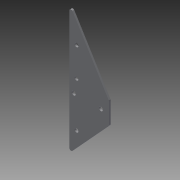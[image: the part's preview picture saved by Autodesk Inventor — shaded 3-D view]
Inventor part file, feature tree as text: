
AUTODESK INVENTOR PART (.ipt)
format: ipt  version: 2013 (Build 170138000, 138)  size: 130,560 bytes
history: native  units: in
note: dims shown in document units (in); Inventor stores cm internally (conversion verified against a paired STEP export)
features: extrude x5, sketch x5, fillet x3
ambient origin geometry x8: Origin, YZ Plane, XZ Plane, XY Plane, X Axis, Y Axis, Z Axis, Center Point
bodies: Solid1 (feature_tree)
feature tree (13):
  extrude  "Extrusion1"  Depth=6.0in
  extrude  "Extrusion2"  Depth=0.28in
  fillet  "Fillet1"  Radius=0.28in
  extrude  "Extrusion3"  Depth=0.75in
  fillet  "Fillet2"  Radius=0.56in
  fillet  "Fillet3"  Radius=0.31in
  extrude  "Extrusion4"  Depth=0.125in
  extrude  "Extrusion5"  Depth=0.266in
  sketch  "Sketch1"  dims[d1=1.5in d2=6.0in]
  sketch  "Sketch2"  dims[d3=0.125in d4=0.0in d5=0.28in d6=0.28in]
  sketch  "Sketch3"  dims[d7=0.75in d8=0.75in d9=0.56in d11=0.31in]
  sketch  "Sketch4"  dims[d12=1.0in d13=0.0in d14=0.125in]
  sketch  "Sketch5"  dims[d15=0.266in d16=0.266in d17=0.5in d18=0.5in d19=1.737in d20=2.0in d21=1.0in d22=0.0in d23=0.125in d24=3.0in d25=2.75in d26=2.75in d27=0.125in d28=0.266in d29=3.125in d30=0.5in d31=1.0in d32=0.0in d33=1.0in d34=0.0in]
